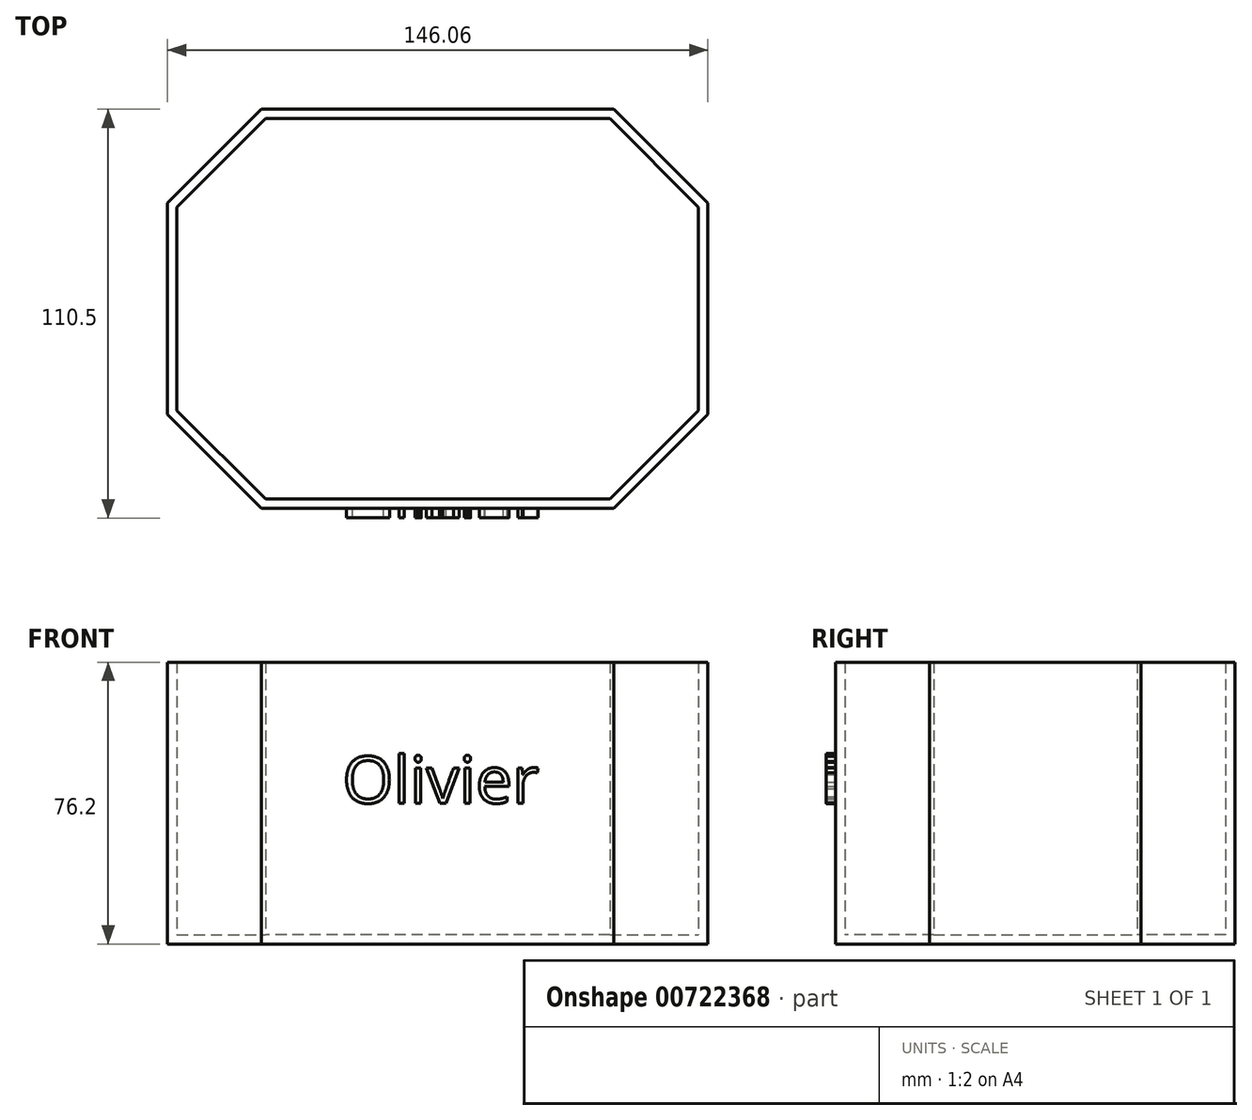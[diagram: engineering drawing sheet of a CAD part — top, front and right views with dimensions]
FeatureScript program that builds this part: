
annotation { "Feature Type Name" : "Feature", "Feature Type Description" : "" }
export const myFeature = defineFeature(function(context is Context, id is Id, definition is map)
    precondition{}
    {
        {
            var Q0;
            Q0=qCreatedBy(makeId("Top.planeOp"),FACE);
            var sketch = newSketch(context, id + "F0", { "sketchPlane" : qUnion([Q0])});
            skLineSegment(sketch, "E0.bottom", {"start": v(47.62, -53.98) * mm, "end": v(-47.62, -53.98) * mm});
            skLineSegment(sketch, "E0.top", {"start": v(47.62, 53.98) * mm, "end": v(-47.63, 53.97) * mm});
            skLineSegment(sketch, "E0.left", {"start": v(73.03, -28.57) * mm, "end": v(73.02, 28.58) * mm});
            skLineSegment(sketch, "E0.right", {"start": v(-73.03, -28.58) * mm, "end": v(-73.03, 28.57) * mm});
            skPoint(sketch, "E0.middle", {"position": v(0, 0) * mm});
            skLineSegment(sketch, "E1", {"start": v(-73.03, 28.57) * mm, "end": v(-47.63, 53.98) * mm});
            skPoint(sketch, "E2.orphan", {"position": v(-73.03, 53.97) * mm});
            skLineSegment(sketch, "E3", {"start": v(47.62, 53.98) * mm, "end": v(73.02, 28.58) * mm});
            skLineSegment(sketch, "E4", {"start": v(73.03, -28.57) * mm, "end": v(47.62, -53.97) * mm});
            skLineSegment(sketch, "E5", {"start": v(-73.03, -28.58) * mm, "end": v(-47.62, -53.98) * mm});
            skPoint(sketch, "E6.orphan", {"position": v(73.02, 53.98) * mm});
            skPoint(sketch, "E7.orphan", {"position": v(-73.03, -53.98) * mm});
            skPoint(sketch, "E8.orphan", {"position": v(73.03, -53.98) * mm});
            skSolve(sketch);
        }
        {
            var Q0;
            Q0=makeQuery(id+"F0.imprint","IMPRINT",FACE,{"disambiguationData":[TD([[makeQuery(id+"F0.imprint","IMPRINT",EDGE,{"derivedFrom":sQuery(id+"F0.wireOp",EDGE,"E0.bottom")}),-1.0]])]});
            var Q1;
            Q1=sQuery(id+"F0.wireOp",EDGE,"E5");
            var Q2;
            Q2=sQuery(id+"F0.wireOp",EDGE,"E0.right");
            var Q3;
            Q3=sQuery(id+"F0.wireOp",EDGE,"E1");
            var Q4;
            Q4=sQuery(id+"F0.wireOp",EDGE,"E0.top");
            var Q5;
            Q5=sQuery(id+"F0.wireOp",EDGE,"E3");
            var Q6;
            Q6=sQuery(id+"F0.wireOp",EDGE,"E0.left");
            var Q7;
            Q7=sQuery(id+"F0.wireOp",EDGE,"E4");
            var Q8;
            Q8=sQuery(id+"F0.wireOp",EDGE,"E0.bottom");
            extrude(context, id + "F1", {"entities" : qUnion([Q0]), "surfaceEntities" : qUnion([Q1, Q2, Q3, Q4, Q5, Q6, Q7, Q8]), "depth" : 76.2 * mm, "offsetDistance" : 25.4 * mm, "hasSecondDirectionDraft" : true, "secondDirectionDraftAngle" : 20 * degree, "secondDirectionDraftPullDirection" : true});
        }
        {
            var Q0;
            Q0=makeQuery(id+"F1.opExtrude","CAP_FACE",FACE,{"disambiguationData":[OSD([sQuery(id+"F0.wireOp",EDGE,"E0.bottom"),sQuery(id+"F0.wireOp",EDGE,"E0.top"),sQuery(id+"F0.wireOp",EDGE,"E0.left"),sQuery(id+"F0.wireOp",EDGE,"E0.right"),sQuery(id+"F0.wireOp",EDGE,"E1"),sQuery(id+"F0.wireOp",EDGE,"E3"),sQuery(id+"F0.wireOp",EDGE,"E4"),sQuery(id+"F0.wireOp",EDGE,"E5")])],"isStart":false});
            shell(context, id + "F2", {"entities" : qUnion([Q0]), "thickness" : 2.54 * mm});
        }
        {
            var Q0;
            Q0=makeQuery(id+"F1.opExtrude","SWEPT_FACE",FACE,{"disambiguationData":[OSD([sQuery(id+"F0.wireOp",EDGE,"E0.bottom")])]});
            var sketch = newSketch(context, id + "F3", { "sketchPlane" : qUnion([Q0])});
            skText(sketch, "E9", { "text": "Olivier", "fontName": "OpenSans-Regular.ttf"});
            const initialGuessF3  = {"E9": [-0.0257, 0.0381, 1, 0, 0.0127]};
            skSetInitialGuess(sketch, initialGuessF3);
            skSolve(sketch);
        }
        {
            var Q0;
            Q0 = qSketchRegion(id + "F3", true);
            extrude(context, id + "F4", {"entities" : qUnion([Q0]), "operationType" : NewBodyOperationType.ADD, "depth" : 2.54 * mm, "offsetDistance" : 25.4 * mm});
        }
    });
